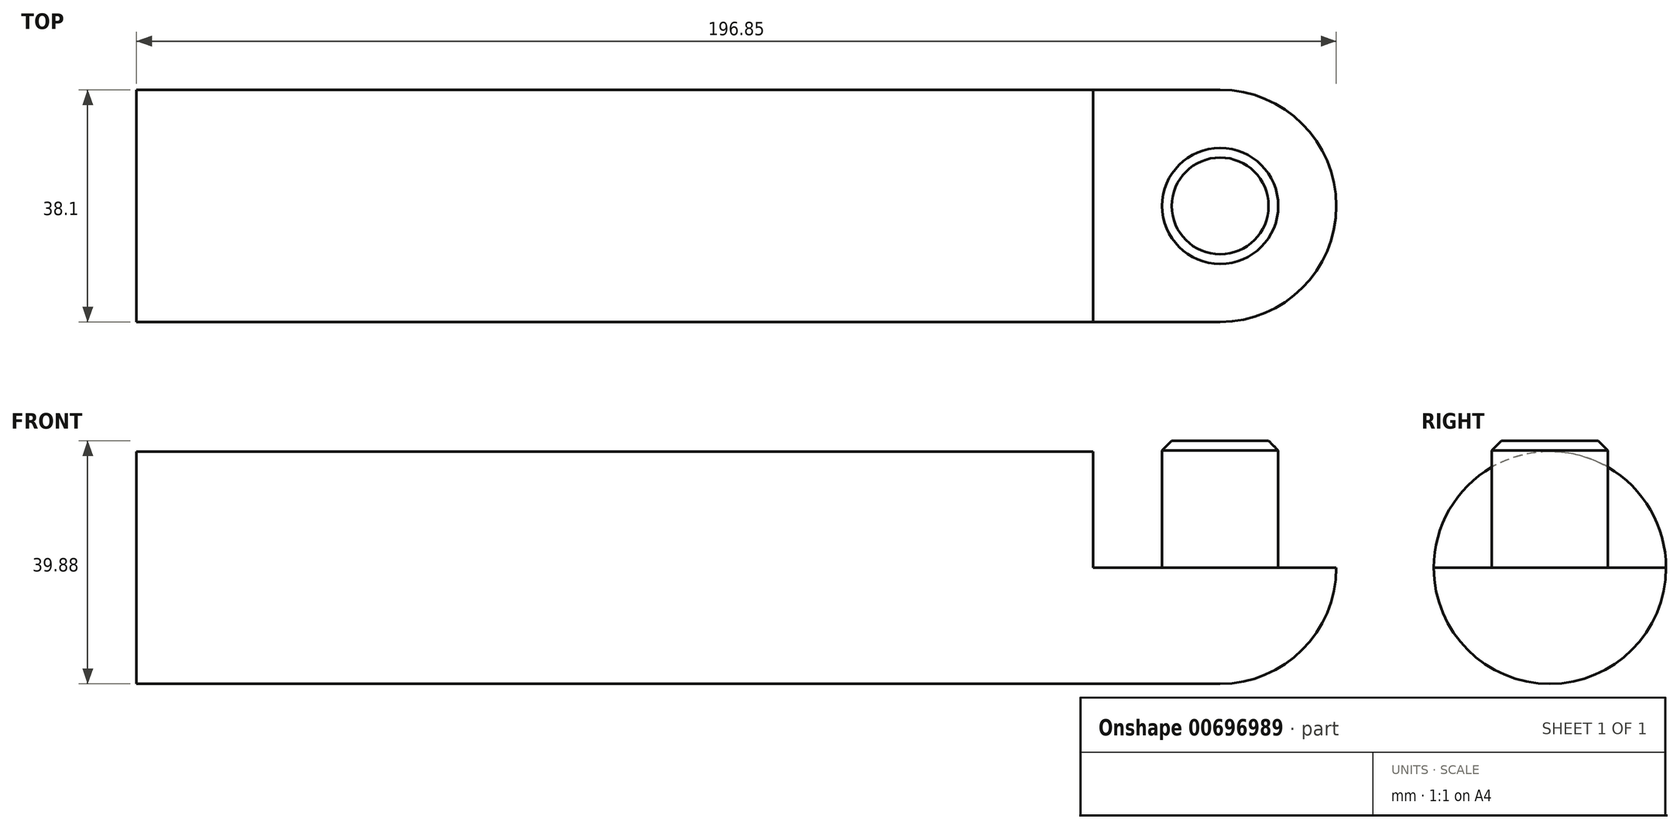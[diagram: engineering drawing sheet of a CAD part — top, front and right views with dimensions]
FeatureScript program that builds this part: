
annotation { "Feature Type Name" : "Feature", "Feature Type Description" : "" }
export const myFeature = defineFeature(function(context is Context, id is Id, definition is map)
    precondition{}
    {
        {
            var Q0;
            Q0=qCreatedBy(makeId("Front.planeOp"),FACE);
            var sketch = newSketch(context, id + "F0", { "sketchPlane" : qUnion([Q0])});
            skLineSegment(sketch, "E0", {"start": v(-98.43, 0) * mm, "end": v(98.42, 0) * mm});
            skLineSegment(sketch, "E1", {"start": v(-98.43, 0) * mm, "end": v(-98.43, 19.05) * mm});
            skLineSegment(sketch, "E2", {"start": v(-98.43, 19.05) * mm, "end": v(79.38, 19.05) * mm});
            skArc(sketch, "E3", {"start": v(98.42, 0) * mm, "mid": v(92.85, 13.47) * mm, "end": v(79.38, 19.05) * mm});
            skPoint(sketch, "E4.orphan", {"position": v(79.38, -19.05) * mm});
            skSolve(sketch);
        }
        {
            var Q0;
            Q0=makeQuery(id+"F0.imprint","IMPRINT",FACE,{"disambiguationData":[TD([[makeQuery(id+"F0.imprint","IMPRINT",EDGE,{"derivedFrom":sQuery(id+"F0.wireOp",EDGE,"E0")}),1.0]])]});
            var Q1;
            Q1=sQuery(id+"F0.wireOp",EDGE,"E0");
            revolve(context, id + "F1", {"entities" : qUnion([Q0]), "axis" : qUnion([Q1]), "revolveType" : RevolveType.FULL});
        }
        {
            var Q0;
            Q0=qCreatedBy(makeId("Top.planeOp"),FACE);
            var sketch = newSketch(context, id + "F2", { "sketchPlane" : qUnion([Q0])});
            skLineSegment(sketch, "E5", {"start": v(-98.43, 19.05) * mm, "end": v(79.38, 19.05) * mm});
            skArc(sketch, "E6", {"start": v(79.38, -19.05) * mm, "mid": v(98.42, 0) * mm, "end": v(79.38, 19.05) * mm});
            skLineSegment(sketch, "E7", {"start": v(79.38, -19.05) * mm, "end": v(-98.43, -19.05) * mm});
            skLineSegment(sketch, "E8", {"start": v(58.55, -19.05) * mm, "end": v(58.55, 19.05) * mm});
            skSolve(sketch);
        }
        {
            var Q0;
            Q0 = qSketchRegion(id + "F2", true);
            extrude(context, id + "F3", {"entities" : qUnion([Q0]), "operationType" : NewBodyOperationType.REMOVE, "depth" : 25.4 * mm, "offsetDistance" : 25.4 * mm});
        }
        {
            var Q0;
            Q0=makeQuery(id+"F3.boolean.opBoolean","COPY",FACE,{"derivedFrom":makeQuery(id+"F3.opExtrude","CAP_FACE",FACE,{"disambiguationData":[OSD([sQuery(id+"F2.wireOp",EDGE,"E5"),sQuery(id+"F2.wireOp",EDGE,"E6"),sQuery(id+"F2.wireOp",EDGE,"E7"),sQuery(id+"F2.wireOp",EDGE,"E8")])],"isStart":true})});
            var sketch = newSketch(context, id + "F4", { "sketchPlane" : qUnion([Q0])});
            skArc(sketch, "E9.0", {"start": v(79.38, -19.05) * mm, "mid": v(98.42, 0) * mm, "end": v(79.38, 19.05) * mm});
            skCircle(sketch, "E10", {"center": v(79.38, 0) * mm, "radius": 9.53 * mm});
            skSolve(sketch);
        }
        {
            var Q0;
            Q0=makeQuery(id+"F4.imprint","IMPRINT",FACE,{"disambiguationData":[TD([[makeQuery(id+"F4.imprint","IMPRINT",EDGE,{"derivedFrom":sQuery(id+"F4.wireOp",EDGE,"E10")}),1.0]])]});
            extrude(context, id + "F5", {"entities" : qUnion([Q0]), "operationType" : NewBodyOperationType.ADD, "depth" : 20.83 * mm, "offsetDistance" : 25.4 * mm});
        }
        {
            var Q0;
            Q0=makeQuery(id+"F5.opExtrude","CAP_EDGE",EDGE,{"disambiguationData":[OSD([sQuery(id+"F4.wireOp",EDGE,"E10")])],"isStart":false});
            chamfer(context, id + "F6", {"entities" : qUnion([Q0]), "width" : 1.59 * mm, "tangentPropagation" : true});
        }
    });
